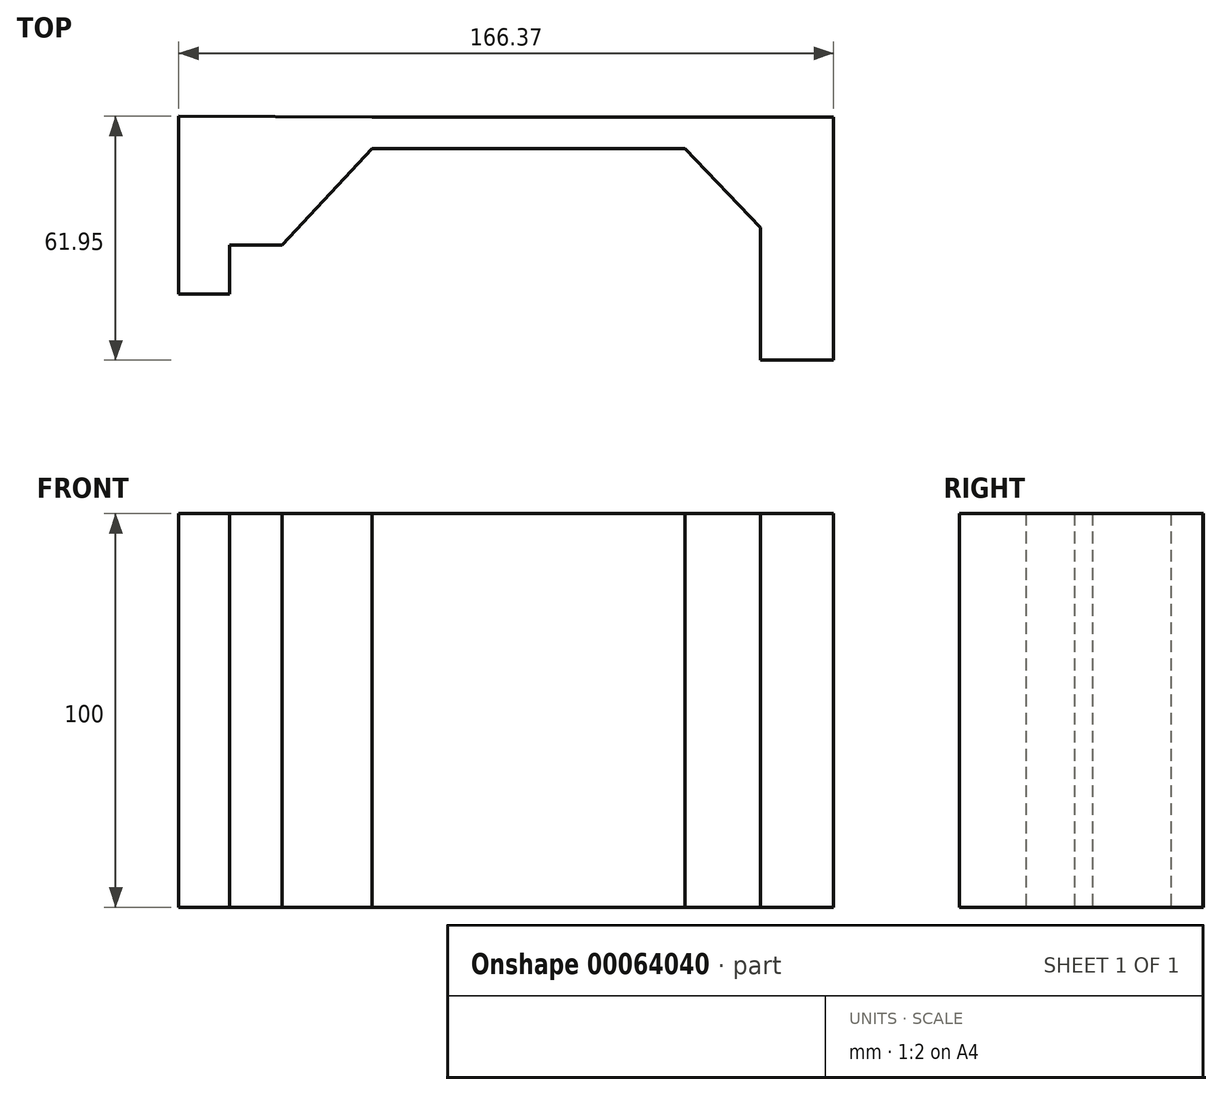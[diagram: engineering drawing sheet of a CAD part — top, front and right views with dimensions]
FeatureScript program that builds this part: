
annotation { "Feature Type Name" : "Feature", "Feature Type Description" : "" }
export const myFeature = defineFeature(function(context is Context, id is Id, definition is map)
    precondition{}
    {
        {
            var Q0;
            Q0=qCreatedBy(makeId("Top.planeOp"),FACE);
            var sketch = newSketch(context, id + "F0", { "sketchPlane" : qUnion([Q0])});
            skLineSegment(sketch, "E0", {"start": v(-62.61, -24.49) * mm, "end": v(-39.75, 0) * mm});
            skLineSegment(sketch, "E1", {"start": v(-39.75, 0) * mm, "end": v(39.75, 0) * mm});
            skLineSegment(sketch, "E2", {"start": v(39.75, 0) * mm, "end": v(59, -20) * mm});
            skLineSegment(sketch, "E3", {"start": v(-62.61, -24.49) * mm, "end": v(39.75, 0) * mm, "construction": true});
            skLineSegment(sketch, "E4", {"start": v(-39.75, 0) * mm, "end": v(59, -20) * mm, "construction": true});
            skPoint(sketch, "E5", {"position": v(0, 0) * mm});
            skLineSegment(sketch, "E6", {"start": v(-39.75, 8.09) * mm, "end": v(39.75, 8.09) * mm});
            skLineSegment(sketch, "E7", {"start": v(-62.61, -24.49) * mm, "end": v(-75.9, -24.49) * mm});
            skLineSegment(sketch, "E8", {"start": v(-75.9, -24.49) * mm, "end": v(-75.9, -36.88) * mm});
            skLineSegment(sketch, "E9", {"start": v(-75.9, -36.88) * mm, "end": v(-88.81, -36.88) * mm});
            skLineSegment(sketch, "E10", {"start": v(-88.81, -36.88) * mm, "end": v(-88.81, 8.24) * mm});
            skLineSegment(sketch, "E11", {"start": v(-88.81, 8.24) * mm, "end": v(-39.75, 8.09) * mm});
            skLineSegment(sketch, "E12", {"start": v(59, -20) * mm, "end": v(59, -53.71) * mm});
            skLineSegment(sketch, "E13", {"start": v(59, -53.71) * mm, "end": v(77.56, -53.71) * mm});
            skLineSegment(sketch, "E14", {"start": v(77.56, -53.71) * mm, "end": v(77.56, 8.09) * mm});
            skLineSegment(sketch, "E15", {"start": v(77.56, 8.09) * mm, "end": v(39.75, 8.09) * mm});
            skSolve(sketch);
        }
        {
            var Q0;
            Q0=makeQuery(id+"F0.imprint","IMPRINT",FACE,{"disambiguationData":[TD([[makeQuery(id+"F0.imprint","IMPRINT",EDGE,{"derivedFrom":sQuery(id+"F0.wireOp",EDGE,"E0")}),1.0]])]});
            extrude(context, id + "F1", {"entities" : qUnion([Q0]), "depth" : 100 * mm, "offsetDistance" : 25 * mm});
        }
    });
